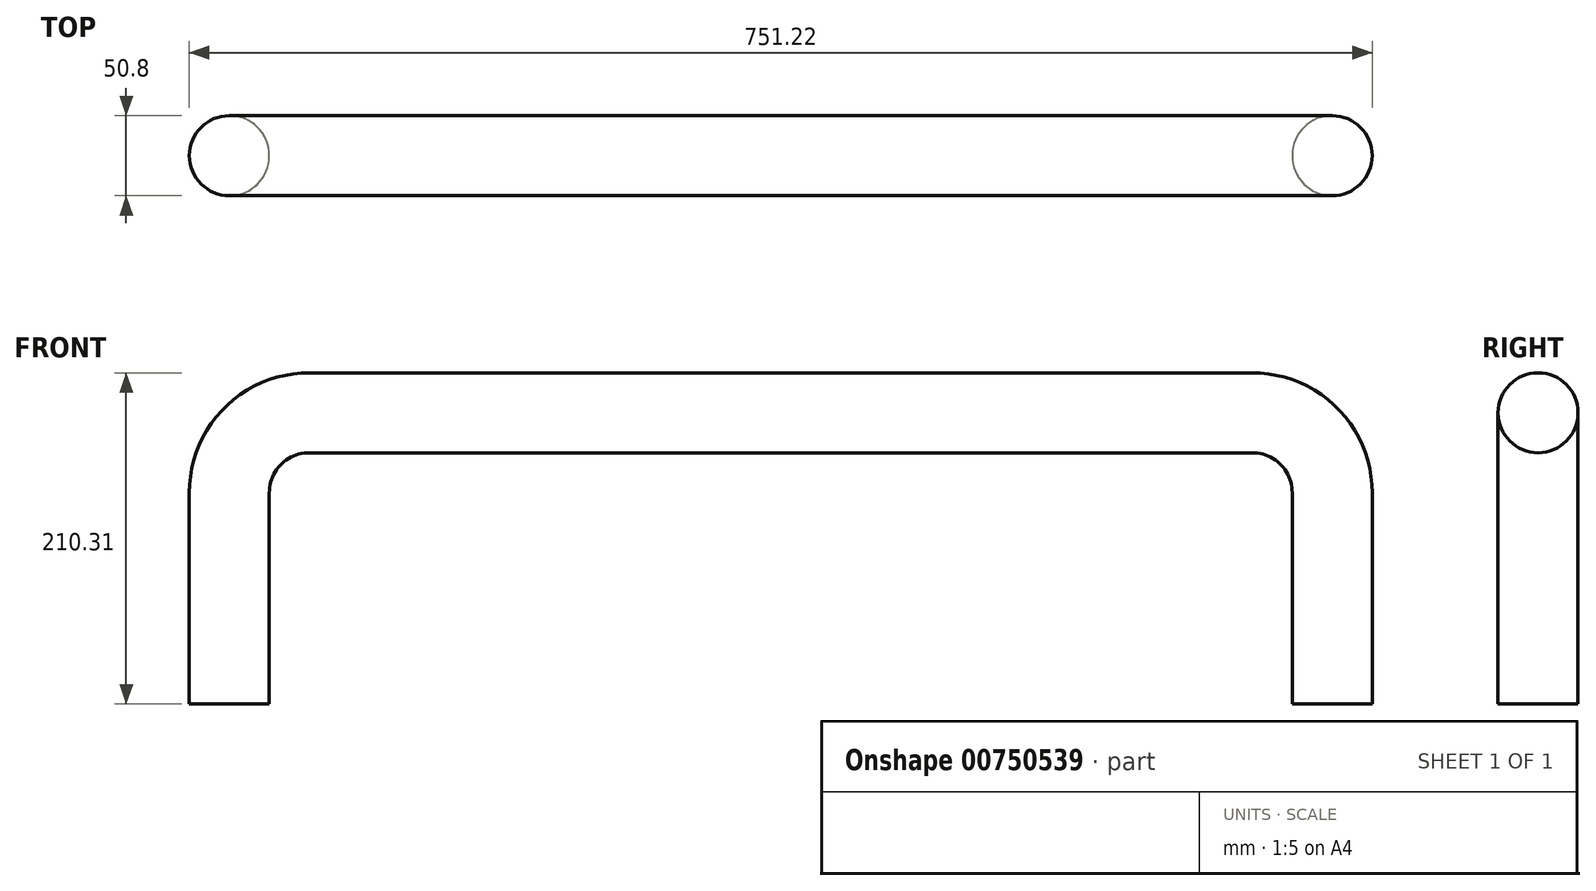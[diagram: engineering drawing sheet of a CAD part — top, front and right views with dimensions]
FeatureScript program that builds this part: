
annotation { "Feature Type Name" : "Feature", "Feature Type Description" : "" }
export const myFeature = defineFeature(function(context is Context, id is Id, definition is map)
    precondition{}
    {
        {
            var Q0;
            Q0=qCreatedBy(makeId("Front.planeOp"),FACE);
            var sketch = newSketch(context, id + "F0", { "sketchPlane" : qUnion([Q0])});
            skLineSegment(sketch, "E0", {"start": v(350.21, 0) * mm, "end": v(350.21, 134.11) * mm});
            skLineSegment(sketch, "E1", {"start": v(299.41, 184.91) * mm, "end": v(-299.41, 184.91) * mm});
            skLineSegment(sketch, "E2", {"start": v(-350.21, 134.11) * mm, "end": v(-350.21, 0) * mm});
            skPoint(sketch, "E3.visualSharp", {"position": v(-350.21, 184.91) * mm});
            skArc(sketch, "E3.filletArc", {"start": v(-299.41, 184.91) * mm, "mid": v(-335.34, 170.03) * mm, "end": v(-350.21, 134.11) * mm});
            skPoint(sketch, "E4.visualSharp", {"position": v(350.21, 184.91) * mm});
            skArc(sketch, "E4.filletArc", {"start": v(350.21, 134.11) * mm, "mid": v(335.34, 170.03) * mm, "end": v(299.41, 184.91) * mm});
            skPoint(sketch, "E5", {"position": v(0, 184.91) * mm});
            skSolve(sketch);
        }
        {
            var Q0;
            Q0=qCreatedBy(makeId("Top.planeOp"),FACE);
            var sketch = newSketch(context, id + "F1", { "sketchPlane" : qUnion([Q0])});
            skCircle(sketch, "E6", {"center": v(350.21, 0) * mm, "radius": 25.4 * mm});
            skSolve(sketch);
        }
        {
            var Q0;
            Q0=makeQuery(id+"F1.imprint","IMPRINT",FACE,{"disambiguationData":[TD([[makeQuery(id+"F1.imprint","IMPRINT",EDGE,{"derivedFrom":sQuery(id+"F1.wireOp",EDGE,"E6")}),1.0]])]});
            var Q1;
            Q1 = qConstructionFilter(qBodyType(qCreatedBy(id + "F0" ,EDGE), BodyType.WIRE), ConstructionObject.NO);
            sweep(context, id + "F2", {"profiles" : qUnion([Q0]), "path" : qUnion([Q1])});
        }
    });
